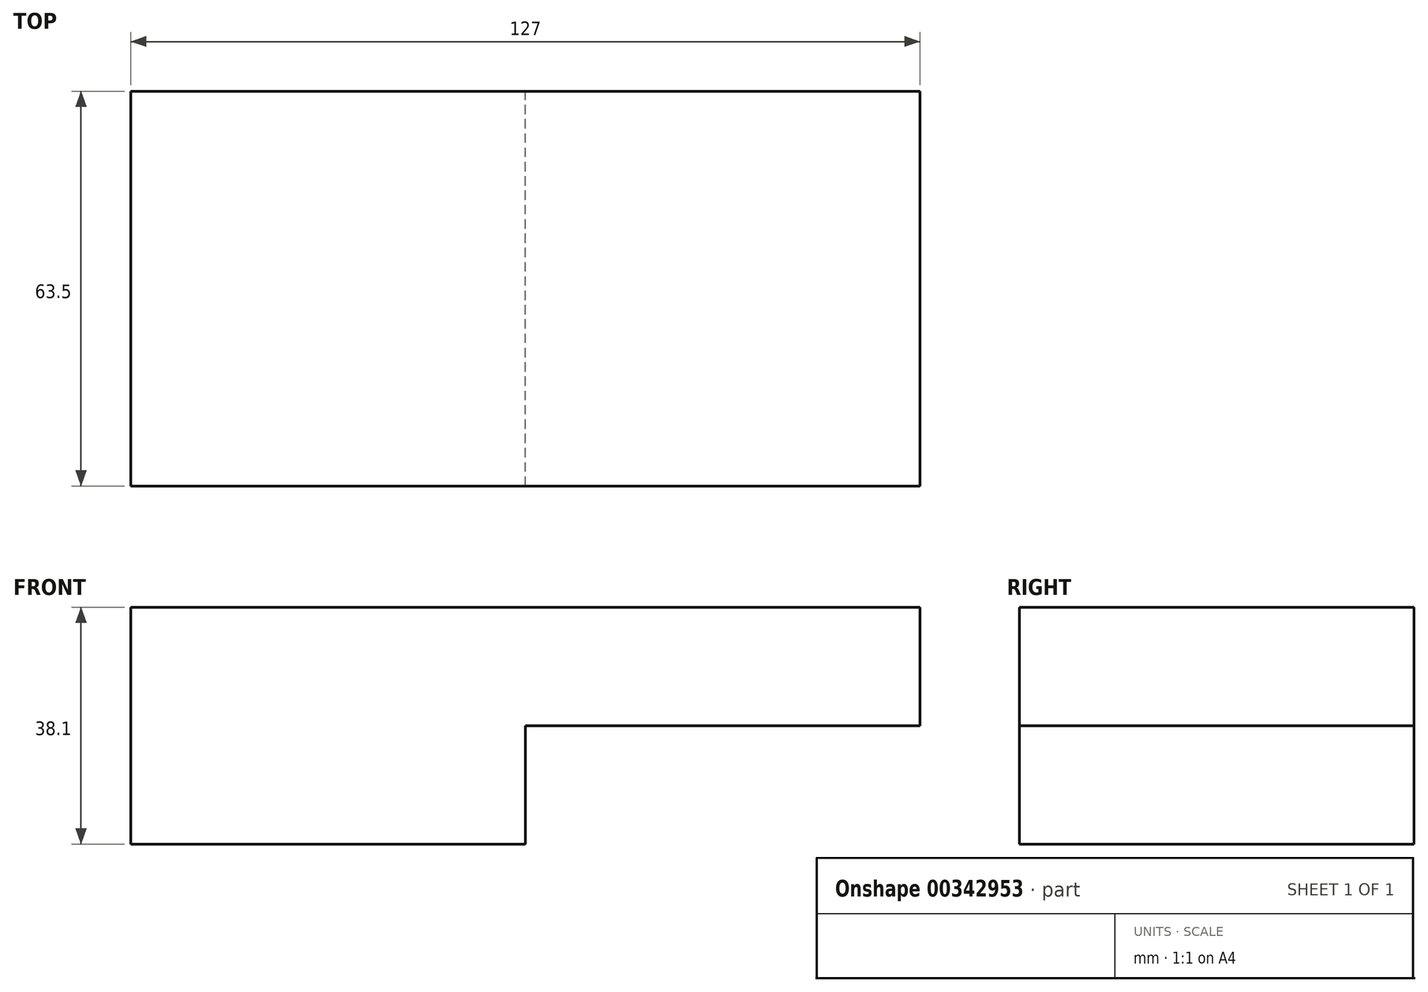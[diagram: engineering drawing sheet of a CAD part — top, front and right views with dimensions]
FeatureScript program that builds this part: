
annotation { "Feature Type Name" : "Feature", "Feature Type Description" : "" }
export const myFeature = defineFeature(function(context is Context, id is Id, definition is map)
    precondition{}
    {
        {
            var Q0;
            Q0=qCreatedBy(makeId("Front.planeOp"),FACE);
            var sketch = newSketch(context, id + "F0", { "sketchPlane" : qUnion([Q0])});
            skLineSegment(sketch, "E0", {"start": v(-63.5, 46.4) * mm, "end": v(63.5, 46.4) * mm});
            skLineSegment(sketch, "E1", {"start": v(-63.5, 46.4) * mm, "end": v(-63.5, 8.3) * mm});
            skLineSegment(sketch, "E2", {"start": v(-63.5, 8.3) * mm, "end": v(0, 8.3) * mm});
            skLineSegment(sketch, "E3", {"start": v(0, 8.3) * mm, "end": v(0, 27.36) * mm});
            skLineSegment(sketch, "E4", {"start": v(0, 27.36) * mm, "end": v(63.5, 27.36) * mm});
            skLineSegment(sketch, "E5", {"start": v(63.5, 27.36) * mm, "end": v(63.5, 46.4) * mm});
            skSolve(sketch);
        }
        {
            var Q0;
            Q0=makeQuery(id+"F0.imprint","IMPRINT",FACE,{"disambiguationData":[TD([[makeQuery(id+"F0.imprint","IMPRINT",EDGE,{"derivedFrom":sQuery(id+"F0.wireOp",EDGE,"E0")}),-1.0]])]});
            extrude(context, id + "F1", {"entities" : qUnion([Q0]), "depth" : 63.5 * mm});
        }
    });
